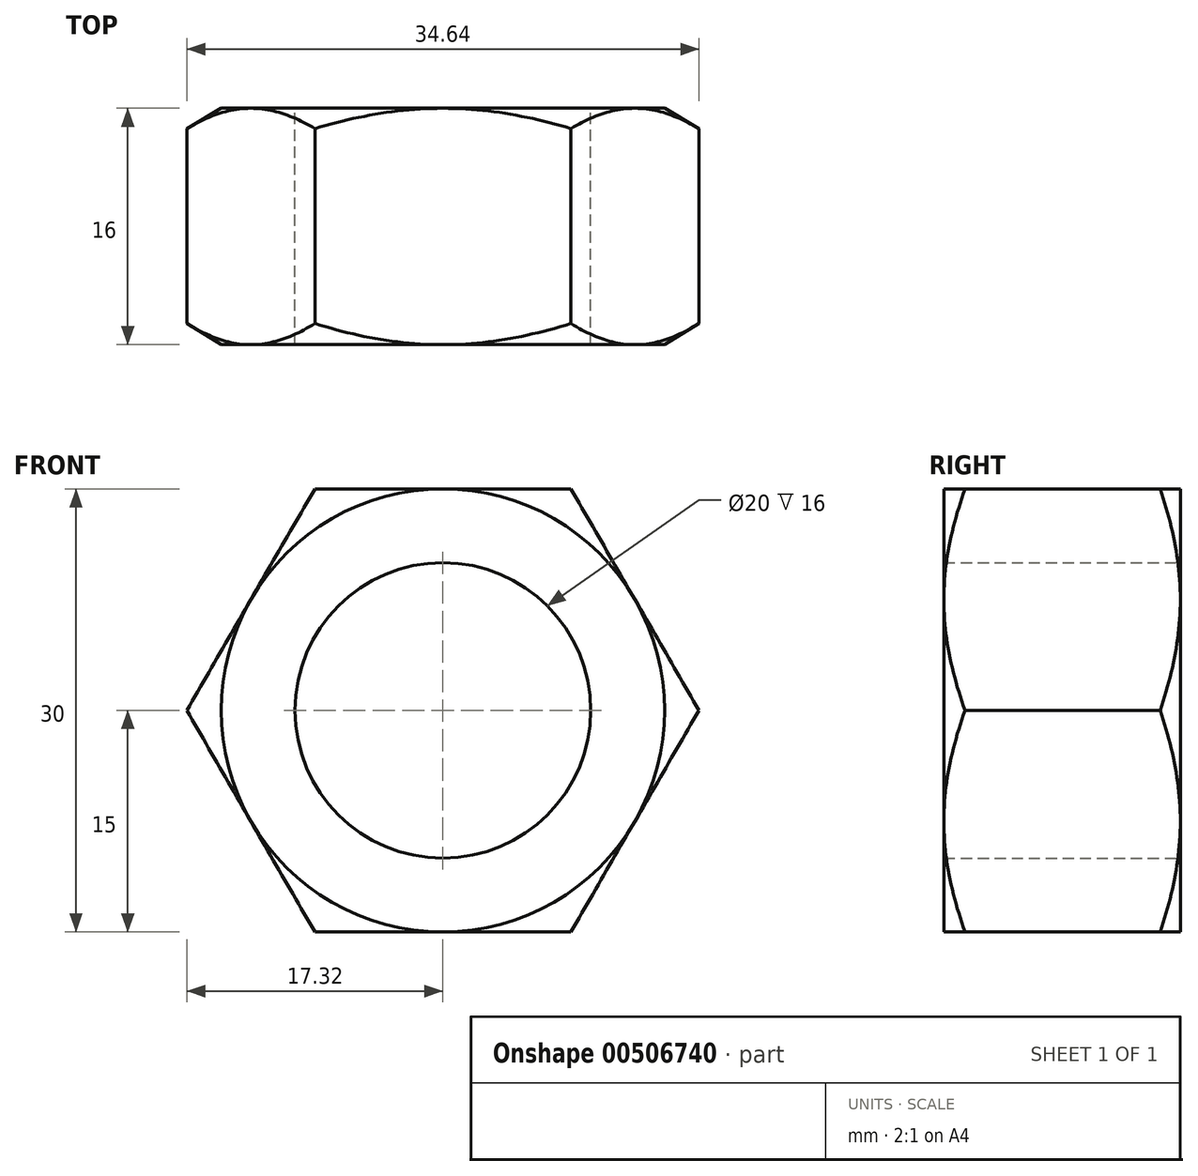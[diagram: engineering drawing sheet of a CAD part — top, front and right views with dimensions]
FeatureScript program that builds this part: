
annotation { "Feature Type Name" : "Feature", "Feature Type Description" : "" }
export const myFeature = defineFeature(function(context is Context, id is Id, definition is map)
    precondition{}
    {
        {
            var Q0;
            Q0=qCreatedBy(makeId("Front.planeOp"),FACE);
            var sketch = newSketch(context, id + "F0", { "sketchPlane" : qUnion([Q0])});
            skCircle(sketch, "E0", {"center": v(0, 0) * mm, "radius": 10 * mm});
            skCircle(sketch, "E1.cCircle", {"center": v(0, 0) * mm, "radius": 15 * mm, "construction": true});
            skLineSegment(sketch, "E1.0", {"start": v(8.66, -15) * mm, "end": v(-8.66, -15) * mm});
            skLineSegment(sketch, "E1.1", {"start": v(-8.66, -15) * mm, "end": v(-17.32, 0) * mm});
            skLineSegment(sketch, "E1.2", {"start": v(-17.32, 0) * mm, "end": v(-8.66, 15) * mm});
            skLineSegment(sketch, "E1.3", {"start": v(-8.66, 15) * mm, "end": v(8.66, 15) * mm});
            skLineSegment(sketch, "E1.4", {"start": v(8.66, 15) * mm, "end": v(17.32, 0) * mm});
            skLineSegment(sketch, "E1.5", {"start": v(17.32, 0) * mm, "end": v(8.66, -15) * mm});
            skPoint(sketch, "E1.0.midPoint", {"position": v(0, -15) * mm});
            skSolve(sketch);
        }
        {
            var Q0;
            Q0=qSketchRegion(id+"F0",true);
            extrude(context, id + "F1", {"entities" : qUnion([Q0]), "depth" : 16 * mm, "offsetDistance" : 25 * mm});
        }
        {
            var Q0;
            Q0=qCreatedBy(makeId("Top.planeOp"),FACE);
            var sketch = newSketch(context, id + "F2", { "sketchPlane" : qUnion([Q0])});
            skLineSegment(sketch, "E2", {"start": v(0, 0) * mm, "end": v(-15, 0) * mm});
            skLineSegment(sketch, "E3", {"start": v(-15, 0) * mm, "end": v(-18.2, -1.89) * mm});
            skLineSegment(sketch, "E4", {"start": v(0, -16) * mm, "end": v(-15, -16) * mm});
            skLineSegment(sketch, "E5", {"start": v(-15, -16) * mm, "end": v(-18.3, -13.96) * mm});
            skLineSegment(sketch, "E6", {"start": v(-18.3, -13.96) * mm, "end": v(-18.26, -16.13) * mm});
            skLineSegment(sketch, "E7", {"start": v(-18.26, -16.13) * mm, "end": v(0, -16.13) * mm});
            skLineSegment(sketch, "E8", {"start": v(0, -16.13) * mm, "end": v(0, -16) * mm});
            skLineSegment(sketch, "E9", {"start": v(-18.2, -1.89) * mm, "end": v(-18.26, 0.28) * mm});
            skLineSegment(sketch, "E10", {"start": v(-18.26, 0.28) * mm, "end": v(0, 0.28) * mm});
            skLineSegment(sketch, "E11", {"start": v(0, 0.28) * mm, "end": v(0, 0) * mm});
            skSolve(sketch);
        }
        {
            var Q0;
            Q0=qSketchRegion(id+"F2",true);
            var Q1;
            Q1=sQuery(id+"F2.wireOp",EDGE,"E11");
            revolve(context, id + "F3", {"operationType" : NewBodyOperationType.REMOVE, "entities" : qUnion([Q0]), "axis" : qUnion([Q1]), "revolveType" : RevolveType.FULL, "oppositeDirection" : true});
        }
    });
